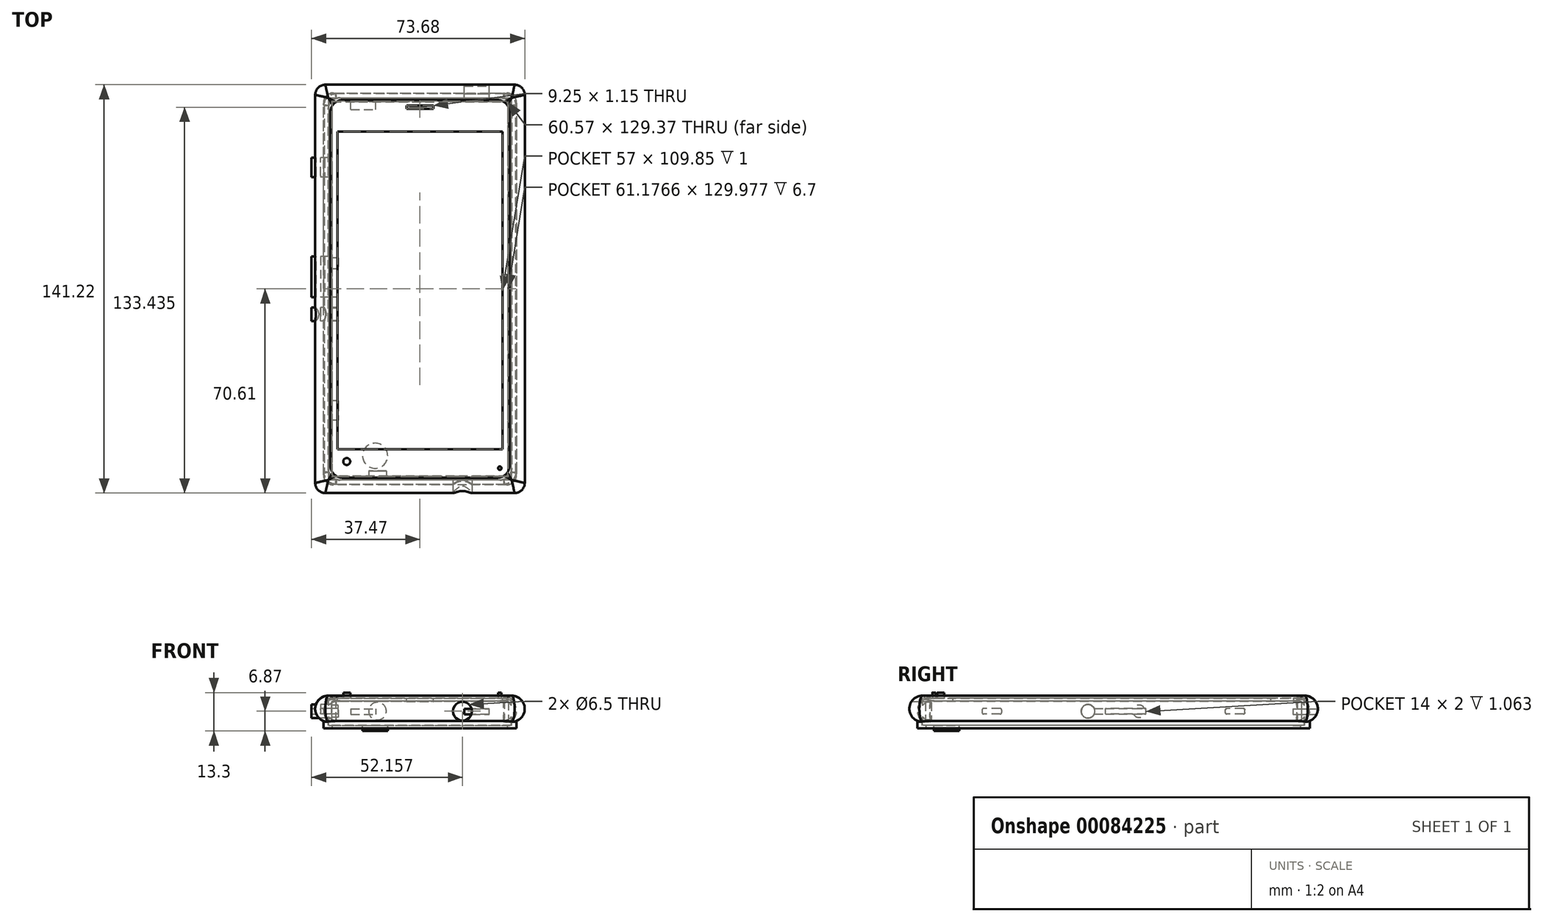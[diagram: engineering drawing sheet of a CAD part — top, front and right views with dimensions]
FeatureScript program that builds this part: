
annotation { "Feature Type Name" : "Feature", "Feature Type Description" : "" }
export const myFeature = defineFeature(function(context is Context, id is Id, definition is map)
    precondition{}
    {
        {
            var Q0;
            Q0=qCreatedBy(makeId("Top.planeOp"),FACE);
            var sketch = newSketch(context, id + "F0", { "sketchPlane" : qUnion([Q0])});
            skLineSegment(sketch, "E0.bottom", {"start": v(31.6, -66) * mm, "end": v(-31.6, -66) * mm});
            skLineSegment(sketch, "E0.top", {"start": v(31.6, 66) * mm, "end": v(-31.6, 66) * mm});
            skLineSegment(sketch, "E0.left", {"start": v(31.6, -66) * mm, "end": v(31.6, 66) * mm});
            skLineSegment(sketch, "E0.right", {"start": v(-31.6, -66) * mm, "end": v(-31.6, 66) * mm});
            skPoint(sketch, "E0.middle", {"position": v(0, 0) * mm});
            skSolve(sketch);
        }
        {
            var Q0;
            Q0=qCreatedBy(makeId("Front.planeOp"),FACE);
            var sketch = newSketch(context, id + "F1", { "sketchPlane" : qUnion([Q0])});
            skLineSegment(sketch, "E1", {"start": v(-31.6, 0) * mm, "end": v(-31.6, 9.3) * mm});
            skLineSegment(sketch, "E2", {"start": v(-31.6, 0) * mm, "end": v(-31.6, 1.5) * mm});
            skLineSegment(sketch, "E3", {"start": v(-31.6, 9.3) * mm, "end": v(-31.6, 8.3) * mm});
            skArc(sketch, "E4", {"start": v(-31.6, 8.3) * mm, "mid": v(-33.1, 4.9) * mm, "end": v(-31.6, 1.5) * mm});
            skLineSegment(sketch, "E5", {"start": v(-33.1, 4.9) * mm, "end": v(-31.6, 4.9) * mm, "construction": true});
            skLineSegment(sketch, "E6", {"start": v(-31.6, 9.3) * mm, "end": v(-30.59, 9.3) * mm});
            skLineSegment(sketch, "E7", {"start": v(-30.59, 9.3) * mm, "end": v(-30.59, 0) * mm});
            skLineSegment(sketch, "E8", {"start": v(-30.59, 0) * mm, "end": v(-31.6, 0) * mm});
            skSolve(sketch);
        }
        {
            var Q0;
            Q0 = qSketchRegion(id + "F1", true);
            var Q1;
            Q1 = qConstructionFilter(qBodyType(qCreatedBy(id + "F0" ,EDGE), BodyType.WIRE), ConstructionObject.NO);
            sweep(context, id + "F2", {"profiles" : qUnion([Q0]), "path" : qUnion([Q1])});
        }
        {
            var Q0;
            Q0=makeQuery(id+"F2.opSweep","SWEPT_FACE",FACE,{"disambiguationData":[OSD([sQuery(id+"F0.wireOp",EDGE,"E0.right"),sQuery(id+"F1.wireOp",EDGE,"E8")])]});
            var sketch = newSketch(context, id + "F3", { "sketchPlane" : qUnion([Q0])});
            skLineSegment(sketch, "E9.0", {"start": v(-31.6, 66) * mm, "end": v(31.6, 66) * mm});
            skLineSegment(sketch, "E10.0", {"start": v(-31.6, -66) * mm, "end": v(-31.6, 66) * mm});
            skLineSegment(sketch, "E11.0", {"start": v(31.6, 66) * mm, "end": v(31.6, -66) * mm});
            skLineSegment(sketch, "E12.0", {"start": v(31.6, -66) * mm, "end": v(-31.6, -66) * mm});
            skSolve(sketch);
        }
        {
            var Q0;
            Q0 = qSketchRegion(id + "F3", true);
            extrude(context, id + "F4", {"entities" : qUnion([Q0]), "operationType" : NewBodyOperationType.ADD, "oppositeDirection" : true, "depth" : 1.5 * mm});
        }
        {
            var Q0;
            Q0=makeQuery(id+"F2.opSweep","SWEPT_FACE",FACE,{"disambiguationData":[OSD([sQuery(id+"F0.wireOp",EDGE,"E0.right"),sQuery(id+"F1.wireOp",EDGE,"E6")])]});
            var sketch = newSketch(context, id + "F5", { "sketchPlane" : qUnion([Q0])});
            skLineSegment(sketch, "E13.0", {"start": v(-31.6, -66) * mm, "end": v(31.6, -66) * mm});
            skLineSegment(sketch, "E14.0", {"start": v(-31.6, 66) * mm, "end": v(-31.6, -66) * mm});
            skLineSegment(sketch, "E15.0", {"start": v(31.6, -66) * mm, "end": v(31.6, 66) * mm});
            skLineSegment(sketch, "E16.0", {"start": v(31.6, 66) * mm, "end": v(-31.6, 66) * mm});
            skSolve(sketch);
        }
        {
            var Q0;
            Q0 = qSketchRegion(id + "F5", true);
            extrude(context, id + "F6", {"entities" : qUnion([Q0]), "operationType" : NewBodyOperationType.ADD, "oppositeDirection" : true, "depth" : 1.1 * mm});
        }
        {
            var Q0;
            Q0=makeQuery(id+"F2.opSweep","MID_CAP_EDGE",EDGE,{"disambiguationData":[OSD([sQuery(id+"F0.wireOp",VERTEX,"E0.right.start"),sQuery(id+"F1.wireOp",EDGE,"E2")])],"capPos":1.0});
            var Q1;
            Q1=makeQuery(id+"F2.opSweep","MID_CAP_EDGE",EDGE,{"disambiguationData":[OSD([sQuery(id+"F0.wireOp",VERTEX,"E0.right.start"),sQuery(id+"F1.wireOp",EDGE,"E4")])],"capPos":1.0});
            var Q2;
            Q2=makeQuery(id+"F2.opSweep","MID_CAP_EDGE",EDGE,{"disambiguationData":[OSD([sQuery(id+"F0.wireOp",VERTEX,"E0.right.start"),sQuery(id+"F1.wireOp",EDGE,"E3")])],"capPos":1.0});
            var Q3;
            Q3=makeQuery(id+"F2.opSweep","MID_CAP_EDGE",EDGE,{"disambiguationData":[OSD([sQuery(id+"F0.wireOp",VERTEX,"E0.left.start"),sQuery(id+"F1.wireOp",EDGE,"E3")])],"capPos":2.0});
            var Q4;
            Q4=makeQuery(id+"F2.opSweep","MID_CAP_EDGE",EDGE,{"disambiguationData":[OSD([sQuery(id+"F0.wireOp",VERTEX,"E0.left.start"),sQuery(id+"F1.wireOp",EDGE,"E4")])],"capPos":2.0});
            var Q5;
            Q5=makeQuery(id+"F2.opSweep","MID_CAP_EDGE",EDGE,{"disambiguationData":[OSD([sQuery(id+"F0.wireOp",VERTEX,"E0.left.start"),sQuery(id+"F1.wireOp",EDGE,"E2")])],"capPos":2.0});
            var Q6;
            Q6=makeQuery(id+"F2.opSweep","MID_CAP_EDGE",EDGE,{"disambiguationData":[OSD([sQuery(id+"F0.wireOp",VERTEX,"E0.left.end"),sQuery(id+"F1.wireOp",EDGE,"E3")])],"capPos":3.0});
            var Q7;
            Q7=makeQuery(id+"F2.opSweep","MID_CAP_EDGE",EDGE,{"disambiguationData":[OSD([sQuery(id+"F0.wireOp",VERTEX,"E0.left.end"),sQuery(id+"F1.wireOp",EDGE,"E4")])],"capPos":3.0});
            var Q8;
            Q8=makeQuery(id+"F2.opSweep","MID_CAP_EDGE",EDGE,{"disambiguationData":[OSD([sQuery(id+"F0.wireOp",VERTEX,"E0.left.end"),sQuery(id+"F1.wireOp",EDGE,"E2")])],"capPos":3.0});
            var Q9;
            Q9=makeQuery(id+"F2.opSweep","CAP_EDGE",EDGE,{"disambiguationData":[OSD([sQuery(id+"F0.wireOp",VERTEX,"E0.right.end"),sQuery(id+"F1.wireOp",EDGE,"E3")])],"isStart":true});
            var Q10;
            Q10=makeQuery(id+"F2.opSweep","CAP_EDGE",EDGE,{"disambiguationData":[OSD([sQuery(id+"F0.wireOp",VERTEX,"E0.right.end"),sQuery(id+"F1.wireOp",EDGE,"E4")])],"isStart":true});
            var Q11;
            Q11=makeQuery(id+"F2.opSweep","CAP_EDGE",EDGE,{"disambiguationData":[OSD([sQuery(id+"F0.wireOp",VERTEX,"E0.right.end"),sQuery(id+"F1.wireOp",EDGE,"E2")])],"isStart":true});
            fillet(context, id + "F7", {"entities" : qUnion([Q0, Q1, Q2, Q3, Q4, Q5, Q6, Q7, Q8, Q9, Q10, Q11]), "radius" : 4.11 * mm, "tangentPropagation" : true, "allowEdgeOverflow" : false});
        }
        {
            var Q0;
            Q0=makeQuery(id+"F2.opSweep","SWEPT_FACE",FACE,{"disambiguationData":[OSD([sQuery(id+"F0.wireOp",EDGE,"E0.right"),sQuery(id+"F1.wireOp",EDGE,"E2")])]});
            var sketch = newSketch(context, id + "F8", { "sketchPlane" : qUnion([Q0])});
            skLineSegment(sketch, "E17.bottom", {"start": v(-39.19, 5.84) * mm, "end": v(-44.89, 5.84) * mm});
            skLineSegment(sketch, "E17.top", {"start": v(-39.19, 3.84) * mm, "end": v(-44.89, 3.84) * mm});
            skLineSegment(sketch, "E17.left", {"start": v(-38.69, 5.34) * mm, "end": v(-38.69, 4.34) * mm});
            skLineSegment(sketch, "E17.right", {"start": v(-45.39, 5.34) * mm, "end": v(-45.39, 4.34) * mm});
            skPoint(sketch, "E17.middle", {"position": v(-42.04, 4.84) * mm});
            skPoint(sketch, "E18.visualSharp", {"position": v(-38.69, 3.84) * mm});
            skArc(sketch, "E18.filletArc", {"start": v(-39.19, 3.84) * mm, "mid": v(-38.83, 4) * mm, "end": v(-38.69, 4.34) * mm});
            skPoint(sketch, "E19.visualSharp", {"position": v(-38.69, 5.84) * mm});
            skArc(sketch, "E19.filletArc", {"start": v(-38.69, 5.34) * mm, "mid": v(-38.83, 5.69) * mm, "end": v(-39.19, 5.84) * mm});
            skPoint(sketch, "E20.visualSharp", {"position": v(-45.39, 5.84) * mm});
            skArc(sketch, "E20.filletArc", {"start": v(-44.89, 5.84) * mm, "mid": v(-45.24, 5.69) * mm, "end": v(-45.39, 5.34) * mm});
            skPoint(sketch, "E21.visualSharp", {"position": v(-45.39, 3.84) * mm});
            skArc(sketch, "E21.filletArc", {"start": v(-45.39, 4.34) * mm, "mid": v(-45.24, 4) * mm, "end": v(-44.89, 3.84) * mm});
            skLineSegment(sketch, "E22.bottom", {"start": v(-11.19, 5.84) * mm, "end": v(2.81, 5.84) * mm});
            skLineSegment(sketch, "E22.top", {"start": v(-11.19, 3.84) * mm, "end": v(2.81, 3.84) * mm});
            skLineSegment(sketch, "E22.left", {"start": v(-11.19, 5.84) * mm, "end": v(-11.19, 3.84) * mm});
            skLineSegment(sketch, "E22.right", {"start": v(2.81, 5.84) * mm, "end": v(2.81, 3.84) * mm});
            skPoint(sketch, "E22.middle", {"position": v(-4.19, 4.84) * mm});
            skCircle(sketch, "E23", {"center": v(8.81, 4.84) * mm, "radius": 2.15 * mm});
            skSolve(sketch);
        }
        {
            var Q0;
            Q0=makeQuery(id+"F8.imprint","IMPRINT",FACE,{"disambiguationData":[TD([[makeQuery(id+"F8.imprint","IMPRINT",EDGE,{"derivedFrom":sQuery(id+"F8.wireOp",EDGE,"E17.bottom")}),1.0]])]});
            var Q1;
            Q1=makeQuery(id+"F8.imprint","IMPRINT",FACE,{"disambiguationData":[TD([[makeQuery(id+"F8.imprint","IMPRINT",EDGE,{"derivedFrom":sQuery(id+"F8.wireOp",EDGE,"E22.bottom")}),-1.0]])]});
            var Q2;
            Q2=makeQuery(id+"F8.imprint","IMPRINT",FACE,{"disambiguationData":[TD([[makeQuery(id+"F8.imprint","IMPRINT",EDGE,{"derivedFrom":sQuery(id+"F8.wireOp",EDGE,"E23")}),1.0]])]});
            extrude(context, id + "F9", {"entities" : qUnion([Q0, Q1, Q2]), "operationType" : NewBodyOperationType.ADD, "depth" : 2.3 * mm});
        }
        {
            var Q0;
            Q0=makeQuery(id+"F4.boolean.opBoolean","MERGE",FACE,{"derivedFrom":[makeQuery(id+"F2.opSweep","SWEPT_FACE",FACE,{"disambiguationData":[OSD([sQuery(id+"F0.wireOp",EDGE,"E0.right"),sQuery(id+"F1.wireOp",EDGE,"E8")])]}),makeQuery(id+"F4.opExtrude","CAP_FACE",FACE,{"disambiguationData":[OSD([sQuery(id+"F3.wireOp",EDGE,"E9.0"),sQuery(id+"F3.wireOp",EDGE,"E10.0"),sQuery(id+"F3.wireOp",EDGE,"E11.0"),sQuery(id+"F3.wireOp",EDGE,"E12.0")])],"isStart":true})]});
            var sketch = newSketch(context, id + "F10", { "sketchPlane" : qUnion([Q0])});
            skCircle(sketch, "E24", {"center": v(-15.5, 57.7) * mm, "radius": 4.35 * mm});
            skSolve(sketch);
        }
        {
            var Q0;
            Q0 = qSketchRegion(id + "F10", true);
            extrude(context, id + "F11", {"entities" : qUnion([Q0]), "operationType" : NewBodyOperationType.ADD, "depth" : 2 * mm});
        }
        {
            var Q0;
            Q0=makeQuery(id+"F6.boolean.opBoolean","MERGE",FACE,{"derivedFrom":[makeQuery(id+"F2.opSweep","SWEPT_FACE",FACE,{"disambiguationData":[OSD([sQuery(id+"F0.wireOp",EDGE,"E0.right"),sQuery(id+"F1.wireOp",EDGE,"E6")])]}),makeQuery(id+"F6.opExtrude","CAP_FACE",FACE,{"disambiguationData":[OSD([sQuery(id+"F5.wireOp",EDGE,"E13.0"),sQuery(id+"F5.wireOp",EDGE,"E14.0"),sQuery(id+"F5.wireOp",EDGE,"E15.0"),sQuery(id+"F5.wireOp",EDGE,"E16.0")])],"isStart":true})]});
            var sketch = newSketch(context, id + "F12", { "sketchPlane" : qUnion([Q0])});
            skCircle(sketch, "E25", {"center": v(27.6, -62) * mm, "radius": 0.6 * mm});
            skCircle(sketch, "E26", {"center": v(-25.3, -59.7) * mm, "radius": 1.2 * mm});
            skSolve(sketch);
        }
        {
            var Q0;
            Q0 = qSketchRegion(id + "F12", true);
            extrude(context, id + "F13", {"entities" : qUnion([Q0]), "operationType" : NewBodyOperationType.ADD, "depth" : 2 * mm});
        }
        {
            var Q0;
            Q0=makeQuery(id+"F6.boolean.opBoolean","MERGE",FACE,{"derivedFrom":[makeQuery(id+"F2.opSweep","SWEPT_FACE",FACE,{"disambiguationData":[OSD([sQuery(id+"F0.wireOp",EDGE,"E0.right"),sQuery(id+"F1.wireOp",EDGE,"E6")])]}),makeQuery(id+"F6.opExtrude","CAP_FACE",FACE,{"disambiguationData":[OSD([sQuery(id+"F5.wireOp",EDGE,"E13.0"),sQuery(id+"F5.wireOp",EDGE,"E14.0"),sQuery(id+"F5.wireOp",EDGE,"E15.0"),sQuery(id+"F5.wireOp",EDGE,"E16.0")])],"isStart":true})]});
            var sketch = newSketch(context, id + "F14", { "sketchPlane" : qUnion([Q0])});
            skLineSegment(sketch, "E27.bottom", {"start": v(-28.5, 54.35) * mm, "end": v(28.5, 54.35) * mm});
            skLineSegment(sketch, "E27.top", {"start": v(-28.5, -55.5) * mm, "end": v(28.5, -55.5) * mm});
            skLineSegment(sketch, "E27.left", {"start": v(-28.5, 54.35) * mm, "end": v(-28.5, -55.5) * mm});
            skLineSegment(sketch, "E27.right", {"start": v(28.5, 54.35) * mm, "end": v(28.5, -55.5) * mm});
            skPoint(sketch, "E27.middle", {"position": v(0, -0.58) * mm});
            skSolve(sketch);
        }
        {
            var Q0;
            Q0 = qSketchRegion(id + "F14", true);
            extrude(context, id + "F15", {"entities" : qUnion([Q0]), "operationType" : NewBodyOperationType.REMOVE, "oppositeDirection" : true, "depth" : 1 * mm});
        }
        {
            var Q0;
            Q0=makeQuery(id+"F6.boolean.opBoolean","MERGE",FACE,{"derivedFrom":[makeQuery(id+"F2.opSweep","SWEPT_FACE",FACE,{"disambiguationData":[OSD([sQuery(id+"F0.wireOp",EDGE,"E0.right"),sQuery(id+"F1.wireOp",EDGE,"E6")])]}),makeQuery(id+"F6.opExtrude","CAP_FACE",FACE,{"disambiguationData":[OSD([sQuery(id+"F5.wireOp",EDGE,"E13.0"),sQuery(id+"F5.wireOp",EDGE,"E14.0"),sQuery(id+"F5.wireOp",EDGE,"E15.0"),sQuery(id+"F5.wireOp",EDGE,"E16.0")])],"isStart":true})]});
            var sketch = newSketch(context, id + "F16", { "sketchPlane" : qUnion([Q0])});
            skLineSegment(sketch, "E28.bottom", {"start": v(-4.62, 63.4) * mm, "end": v(4.63, 63.4) * mm});
            skLineSegment(sketch, "E28.top", {"start": v(-4.62, 62.25) * mm, "end": v(4.63, 62.25) * mm});
            skLineSegment(sketch, "E28.left", {"start": v(-4.62, 63.4) * mm, "end": v(-4.62, 62.25) * mm});
            skLineSegment(sketch, "E28.right", {"start": v(4.63, 63.4) * mm, "end": v(4.63, 62.25) * mm});
            skPoint(sketch, "E28.middle", {"position": v(0, 62.82) * mm});
            skPoint(sketch, "E28.middle.positionSnap0", {"position": v(0, 54.35) * mm});
            skPoint(sketch, "E28.centerSnap0", {"position": v(0, 54.35) * mm});
            skSolve(sketch);
        }
        {
            var Q0;
            Q0 = qSketchRegion(id + "F16", true);
            extrude(context, id + "F17", {"entities" : qUnion([Q0]), "operationType" : NewBodyOperationType.REMOVE, "oppositeDirection" : true, "depth" : 2 * mm});
        }
        {
            var Q0;
            Q0=makeQuery(id+"F2.opSweep","SWEPT_FACE",FACE,{"disambiguationData":[OSD([sQuery(id+"F0.wireOp",EDGE,"E0.bottom"),sQuery(id+"F1.wireOp",EDGE,"E2")])]});
            var sketch = newSketch(context, id + "F18", { "sketchPlane" : qUnion([Q0])});
            skCircle(sketch, "E29", {"center": v(14.69, 4.87) * mm, "radius": 3.05 * mm});
            skSolve(sketch);
        }
        {
            var Q0;
            Q0 = qSketchRegion(id + "F18", true);
            extrude(context, id + "F19", {"entities" : qUnion([Q0]), "operationType" : NewBodyOperationType.ADD, "depth" : 2 * mm});
        }
        {
            var Q0;
            Q0=qCreatedBy(makeId("Front.planeOp"),FACE);
            var sketch = newSketch(context, id + "F20", { "sketchPlane" : qUnion([Q0])});
            skLineSegment(sketch, "E30.0", {"start": v(31.7, 0) * mm, "end": v(31.7, 1.47) * mm, "construction": true});
            skLineSegment(sketch, "E31.0", {"start": v(31.6, -0.1) * mm, "end": v(27.49, -0.1) * mm, "construction": true});
            skLineSegment(sketch, "E32", {"start": v(30.29, -0.1) * mm, "end": v(30.29, -1.05) * mm});
            skLineSegment(sketch, "E33", {"start": v(30.29, -1.05) * mm, "end": v(33.38, -1.05) * mm});
            skLineSegment(sketch, "E34", {"start": v(33.38, -1.05) * mm, "end": v(33.38, 1.47) * mm});
            skLineSegment(sketch, "E35", {"start": v(33.38, 1.47) * mm, "end": v(31.7, 1.47) * mm});
            skLineSegment(sketch, "E36", {"start": v(31.7, -0.1) * mm, "end": v(30.29, -0.1) * mm});
            skLineSegment(sketch, "E37", {"start": v(30.29, -0.1) * mm, "end": v(31.7, -0.1) * mm});
            skLineSegment(sketch, "E38", {"start": v(31.7, 1.47) * mm, "end": v(31.7, -0.1) * mm});
            skArc(sketch, "E39", {"start": v(31.7, 1.47) * mm, "mid": v(33.3, 4.93) * mm, "end": v(31.7, 8.4) * mm});
            skArc(sketch, "E40", {"start": v(33.38, 1.47) * mm, "mid": v(36.04, 6.93) * mm, "end": v(30.9, 10.16) * mm});
            skLineSegment(sketch, "E41", {"start": v(31.7, 8.4) * mm, "end": v(31.7, 9.38) * mm});
            skLineSegment(sketch, "E42", {"start": v(30.9, 10.16) * mm, "end": v(30.9, 9.38) * mm});
            skLineSegment(sketch, "E43", {"start": v(30.9, 9.38) * mm, "end": v(31.7, 9.38) * mm});
            skSolve(sketch);
        }
        {
            var Q0;
            Q0 = qSketchRegion(id + "F20", true);
            var Q1;
            Q1 = qConstructionFilter(qBodyType(qCreatedBy(id + "F0" ,EDGE), BodyType.WIRE), ConstructionObject.NO);
            sweep(context, id + "F21", {"profiles" : qUnion([Q0]), "path" : qUnion([Q1])});
        }
        {
            var Q0;
            Q0=makeQuery(id+"F21.opSweep","CAP_EDGE",EDGE,{"disambiguationData":[OSD([sQuery(id+"F0.wireOp",VERTEX,"E0.left.end"),sQuery(id+"F20.wireOp",EDGE,"E34")])],"isStart":true});
            var Q1;
            Q1=makeQuery(id+"F21.opSweep","CAP_EDGE",EDGE,{"disambiguationData":[OSD([sQuery(id+"F0.wireOp",VERTEX,"E0.left.end"),sQuery(id+"F20.wireOp",EDGE,"E40")])],"isStart":true});
            var Q2;
            Q2=makeQuery(id+"F21.opSweep","MID_CAP_EDGE",EDGE,{"disambiguationData":[OSD([sQuery(id+"F0.wireOp",VERTEX,"E0.right.end"),sQuery(id+"F20.wireOp",EDGE,"E34")])],"capPos":3.0});
            var Q3;
            Q3=makeQuery(id+"F21.opSweep","MID_CAP_EDGE",EDGE,{"disambiguationData":[OSD([sQuery(id+"F0.wireOp",VERTEX,"E0.right.end"),sQuery(id+"F20.wireOp",EDGE,"E40")])],"capPos":3.0});
            var Q4;
            Q4=makeQuery(id+"F21.opSweep","MID_CAP_EDGE",EDGE,{"disambiguationData":[OSD([sQuery(id+"F0.wireOp",VERTEX,"E0.right.start"),sQuery(id+"F20.wireOp",EDGE,"E34")])],"capPos":2.0});
            var Q5;
            Q5=makeQuery(id+"F21.opSweep","MID_CAP_EDGE",EDGE,{"disambiguationData":[OSD([sQuery(id+"F0.wireOp",VERTEX,"E0.right.start"),sQuery(id+"F20.wireOp",EDGE,"E40")])],"capPos":2.0});
            var Q6;
            Q6=makeQuery(id+"F21.opSweep","MID_CAP_EDGE",EDGE,{"disambiguationData":[OSD([sQuery(id+"F0.wireOp",VERTEX,"E0.left.start"),sQuery(id+"F20.wireOp",EDGE,"E34")])],"capPos":1.0});
            var Q7;
            Q7=makeQuery(id+"F21.opSweep","MID_CAP_EDGE",EDGE,{"disambiguationData":[OSD([sQuery(id+"F0.wireOp",VERTEX,"E0.left.start"),sQuery(id+"F20.wireOp",EDGE,"E40")])],"capPos":1.0});
            fillet(context, id + "F22", {"entities" : qUnion([Q0, Q1, Q2, Q3, Q4, Q5, Q6, Q7]), "radius" : 3.5 * mm, "tangentPropagation" : true, "allowEdgeOverflow" : false});
        }
        {
            var Q0;
            Q0=makeQuery(id+"F21.opSweep","CAP_EDGE",EDGE,{"disambiguationData":[OSD([sQuery(id+"F0.wireOp",VERTEX,"E0.left.end"),sQuery(id+"F20.wireOp",EDGE,"E38")])],"isStart":true});
            var Q1;
            Q1=makeQuery(id+"F21.opSweep","CAP_EDGE",EDGE,{"disambiguationData":[OSD([sQuery(id+"F0.wireOp",VERTEX,"E0.left.end"),sQuery(id+"F20.wireOp",EDGE,"E39")])],"isStart":true});
            var Q2;
            Q2=makeQuery(id+"F21.opSweep","MID_CAP_EDGE",EDGE,{"disambiguationData":[OSD([sQuery(id+"F0.wireOp",VERTEX,"E0.left.start"),sQuery(id+"F20.wireOp",EDGE,"E38")])],"capPos":1.0});
            var Q3;
            Q3=makeQuery(id+"F21.opSweep","MID_CAP_EDGE",EDGE,{"disambiguationData":[OSD([sQuery(id+"F0.wireOp",VERTEX,"E0.left.start"),sQuery(id+"F20.wireOp",EDGE,"E39")])],"capPos":1.0});
            var Q4;
            Q4=makeQuery(id+"F21.opSweep","MID_CAP_EDGE",EDGE,{"disambiguationData":[OSD([sQuery(id+"F0.wireOp",VERTEX,"E0.right.start"),sQuery(id+"F20.wireOp",EDGE,"E38")])],"capPos":2.0});
            var Q5;
            Q5=makeQuery(id+"F21.opSweep","MID_CAP_EDGE",EDGE,{"disambiguationData":[OSD([sQuery(id+"F0.wireOp",VERTEX,"E0.right.start"),sQuery(id+"F20.wireOp",EDGE,"E39")])],"capPos":2.0});
            var Q6;
            Q6=makeQuery(id+"F21.opSweep","MID_CAP_EDGE",EDGE,{"disambiguationData":[OSD([sQuery(id+"F0.wireOp",VERTEX,"E0.right.end"),sQuery(id+"F20.wireOp",EDGE,"E38")])],"capPos":3.0});
            var Q7;
            Q7=makeQuery(id+"F21.opSweep","MID_CAP_EDGE",EDGE,{"disambiguationData":[OSD([sQuery(id+"F0.wireOp",VERTEX,"E0.right.end"),sQuery(id+"F20.wireOp",EDGE,"E39")])],"capPos":3.0});
            var Q8;
            Q8=makeQuery(id+"F21.opSweep","MID_CAP_EDGE",EDGE,{"disambiguationData":[OSD([sQuery(id+"F0.wireOp",VERTEX,"E0.right.end"),sQuery(id+"F20.wireOp",EDGE,"E42")])],"capPos":3.0});
            var Q9;
            Q9=makeQuery(id+"F21.opSweep","MID_CAP_EDGE",EDGE,{"disambiguationData":[OSD([sQuery(id+"F0.wireOp",VERTEX,"E0.right.end"),sQuery(id+"F20.wireOp",EDGE,"E41")])],"capPos":3.0});
            var Q10;
            Q10=makeQuery(id+"F21.opSweep","CAP_EDGE",EDGE,{"disambiguationData":[OSD([sQuery(id+"F0.wireOp",VERTEX,"E0.left.end"),sQuery(id+"F20.wireOp",EDGE,"E41")])],"isStart":true});
            var Q11;
            Q11=makeQuery(id+"F21.opSweep","CAP_EDGE",EDGE,{"disambiguationData":[OSD([sQuery(id+"F0.wireOp",VERTEX,"E0.left.end"),sQuery(id+"F20.wireOp",EDGE,"E42")])],"isStart":true});
            var Q12;
            Q12=makeQuery(id+"F21.opSweep","MID_CAP_EDGE",EDGE,{"disambiguationData":[OSD([sQuery(id+"F0.wireOp",VERTEX,"E0.left.start"),sQuery(id+"F20.wireOp",EDGE,"E41")])],"capPos":1.0});
            var Q13;
            Q13=makeQuery(id+"F21.opSweep","MID_CAP_EDGE",EDGE,{"disambiguationData":[OSD([sQuery(id+"F0.wireOp",VERTEX,"E0.left.start"),sQuery(id+"F20.wireOp",EDGE,"E42")])],"capPos":1.0});
            var Q14;
            Q14=makeQuery(id+"F21.opSweep","MID_CAP_EDGE",EDGE,{"disambiguationData":[OSD([sQuery(id+"F0.wireOp",VERTEX,"E0.right.start"),sQuery(id+"F20.wireOp",EDGE,"E41")])],"capPos":2.0});
            var Q15;
            Q15=makeQuery(id+"F21.opSweep","MID_CAP_EDGE",EDGE,{"disambiguationData":[OSD([sQuery(id+"F0.wireOp",VERTEX,"E0.right.start"),sQuery(id+"F20.wireOp",EDGE,"E42")])],"capPos":2.0});
            fillet(context, id + "F23", {"entities" : qUnion([Q0, Q1, Q2, Q3, Q4, Q5, Q6, Q7, Q8, Q9, Q10, Q11, Q12, Q13, Q14, Q15]), "radius" : 4.11 * mm, "tangentPropagation" : true, "allowEdgeOverflow" : false});
        }
        {
            var Q0;
            Q0=makeQuery(id+"F2.opSweep","SWEPT_FACE",FACE,{"disambiguationData":[OSD([sQuery(id+"F0.wireOp",EDGE,"E0.top"),sQuery(id+"F1.wireOp",EDGE,"E2")])]});
            var sketch = newSketch(context, id + "F24", { "sketchPlane" : qUnion([Q0])});
            skLineSegment(sketch, "E44.bottom", {"start": v(-23.92, 5.64) * mm, "end": v(-15.3, 5.64) * mm});
            skLineSegment(sketch, "E44.top", {"start": v(-23.92, 3.74) * mm, "end": v(-15.3, 3.74) * mm});
            skLineSegment(sketch, "E44.left", {"start": v(-23.92, 5.64) * mm, "end": v(-23.92, 3.74) * mm});
            skLineSegment(sketch, "E44.right", {"start": v(-15.3, 5.64) * mm, "end": v(-15.3, 3.74) * mm});
            skSolve(sketch);
        }
        {
            var Q0;
            Q0 = qSketchRegion(id + "F24", true);
            extrude(context, id + "F25", {"entities" : qUnion([Q0]), "operationType" : NewBodyOperationType.ADD, "depth" : 3 * mm});
        }
        {
            var Q0;
            Q0=makeQuery(id+"F21.opSweep","SWEPT_FACE",FACE,{"disambiguationData":[OSD([sQuery(id+"F0.wireOp",EDGE,"E0.right"),sQuery(id+"F20.wireOp",EDGE,"E34")])]});
            var sketch = newSketch(context, id + "F26", { "sketchPlane" : qUnion([Q0])});
            skLineSegment(sketch, "E45.0", {"start": v(-39.19, 5.84) * mm, "end": v(-44.89, 5.84) * mm});
            skArc(sketch, "E46.0", {"start": v(-44.89, 5.84) * mm, "mid": v(-45.24, 5.69) * mm, "end": v(-45.39, 5.34) * mm});
            skLineSegment(sketch, "E47.0", {"start": v(-45.39, 5.34) * mm, "end": v(-45.39, 4.34) * mm});
            skLineSegment(sketch, "E48.0", {"start": v(-39.19, 3.84) * mm, "end": v(-44.89, 3.84) * mm});
            skArc(sketch, "E49.0", {"start": v(-39.19, 3.84) * mm, "mid": v(-38.83, 4) * mm, "end": v(-38.69, 4.34) * mm});
            skLineSegment(sketch, "E50.0", {"start": v(-38.69, 5.34) * mm, "end": v(-38.69, 4.34) * mm});
            skArc(sketch, "E51.0", {"start": v(-38.69, 5.34) * mm, "mid": v(-38.83, 5.69) * mm, "end": v(-39.19, 5.84) * mm});
            skLineSegment(sketch, "E52.0", {"start": v(-11.19, 5.84) * mm, "end": v(-11.19, 3.84) * mm});
            skLineSegment(sketch, "E53.0", {"start": v(-11.19, 5.84) * mm, "end": v(2.81, 5.84) * mm});
            skLineSegment(sketch, "E54.0", {"start": v(-11.19, 3.84) * mm, "end": v(2.81, 3.84) * mm});
            skLineSegment(sketch, "E55.0", {"start": v(2.81, 5.84) * mm, "end": v(2.81, 3.84) * mm});
            skArc(sketch, "E56.0", {"start": v(-45.39, 4.34) * mm, "mid": v(-45.24, 4) * mm, "end": v(-44.89, 3.84) * mm});
            skCircle(sketch, "E57.0", {"center": v(8.81, 4.84) * mm, "radius": 2.35 * mm});
            skSolve(sketch);
        }
        {
            var Q0;
            Q0 = qSketchRegion(id + "F26", true);
            extrude(context, id + "F27", {"entities" : qUnion([Q0]), "operationType" : NewBodyOperationType.ADD, "depth" : 4.1 * mm});
        }
        {
            var Q0;
            Q0=makeQuery(id+"F21.opSweep","SWEPT_FACE",FACE,{"disambiguationData":[OSD([sQuery(id+"F0.wireOp",EDGE,"E0.bottom"),sQuery(id+"F20.wireOp",EDGE,"E34")])]});
            var sketch = newSketch(context, id + "F28", { "sketchPlane" : qUnion([Q0])});
            skCircle(sketch, "E58.0", {"center": v(14.69, 4.87) * mm, "radius": 3.25 * mm});
            skSolve(sketch);
        }
        {
            var Q0;
            Q0 = qSketchRegion(id + "F28", true);
            extrude(context, id + "F29", {"entities" : qUnion([Q0]), "operationType" : NewBodyOperationType.REMOVE, "endBound" : BoundingType.SYMMETRIC, "oppositeDirection" : true, "depth" : 8.1 * mm});
        }
        {
            var Q0;
            Q0 = qSketchRegion(id + "F26", true);
            extrude(context, id + "F30", {"entities" : qUnion([Q0]), "operationType" : NewBodyOperationType.REMOVE, "oppositeDirection" : true, "depth" : 6.6 * mm});
        }
        {
            var Q0;
            Q0=makeQuery(id+"F30.boolean.opBoolean","COPY",FACE,{"derivedFrom":makeQuery(id+"F30.opExtrude","CAP_FACE",FACE,{"disambiguationData":[OSD([sQuery(id+"F26.wireOp",EDGE,"E57.0")])],"isStart":true})});
            var Q1;
            Q1=makeQuery(id+"F30.boolean.opBoolean","COPY",FACE,{"derivedFrom":makeQuery(id+"F30.opExtrude","CAP_FACE",FACE,{"disambiguationData":[OSD([sQuery(id+"F26.wireOp",EDGE,"E52.0"),sQuery(id+"F26.wireOp",EDGE,"E53.0"),sQuery(id+"F26.wireOp",EDGE,"E54.0"),sQuery(id+"F26.wireOp",EDGE,"E55.0")])],"isStart":true})});
            var Q2;
            Q2=makeQuery(id+"F30.boolean.opBoolean","COPY",FACE,{"derivedFrom":makeQuery(id+"F30.opExtrude","CAP_FACE",FACE,{"disambiguationData":[OSD([sQuery(id+"F26.wireOp",EDGE,"E45.0"),sQuery(id+"F26.wireOp",EDGE,"E46.0"),sQuery(id+"F26.wireOp",EDGE,"E47.0"),sQuery(id+"F26.wireOp",EDGE,"E48.0"),sQuery(id+"F26.wireOp",EDGE,"E49.0"),sQuery(id+"F26.wireOp",EDGE,"E50.0"),sQuery(id+"F26.wireOp",EDGE,"E51.0"),sQuery(id+"F26.wireOp",EDGE,"E56.0")])],"isStart":true})});
            extrude(context, id + "F31", {"entities" : qUnion([Q0, Q1, Q2]), "operationType" : NewBodyOperationType.REMOVE, "oppositeDirection" : true, "depth" : .9 * mm});
        }
        {
            var Q0;
            Q0=makeQuery(id+"F21.opSweep","SWEPT_FACE",FACE,{"disambiguationData":[OSD([sQuery(id+"F0.wireOp",EDGE,"E0.top"),sQuery(id+"F20.wireOp",EDGE,"E34")])]});
            var sketch = newSketch(context, id + "F32", { "sketchPlane" : qUnion([Q0])});
            skLineSegment(sketch, "E59.0", {"start": v(-23.92, 5.64) * mm, "end": v(-23.92, 3.74) * mm});
            skLineSegment(sketch, "E60.0", {"start": v(-23.92, 5.64) * mm, "end": v(-15.3, 5.64) * mm});
            skLineSegment(sketch, "E61.0", {"start": v(-15.3, 5.64) * mm, "end": v(-15.3, 3.74) * mm});
            skLineSegment(sketch, "E62.0", {"start": v(-23.92, 3.74) * mm, "end": v(-15.3, 3.74) * mm});
            skSolve(sketch);
        }
        {
            var Q0;
            Q0 = qSketchRegion(id + "F32", true);
            extrude(context, id + "F33", {"entities" : qUnion([Q0]), "operationType" : NewBodyOperationType.REMOVE, "endBound" : BoundingType.SYMMETRIC, "oppositeDirection" : true, "depth" : 17 * mm});
        }
    });
